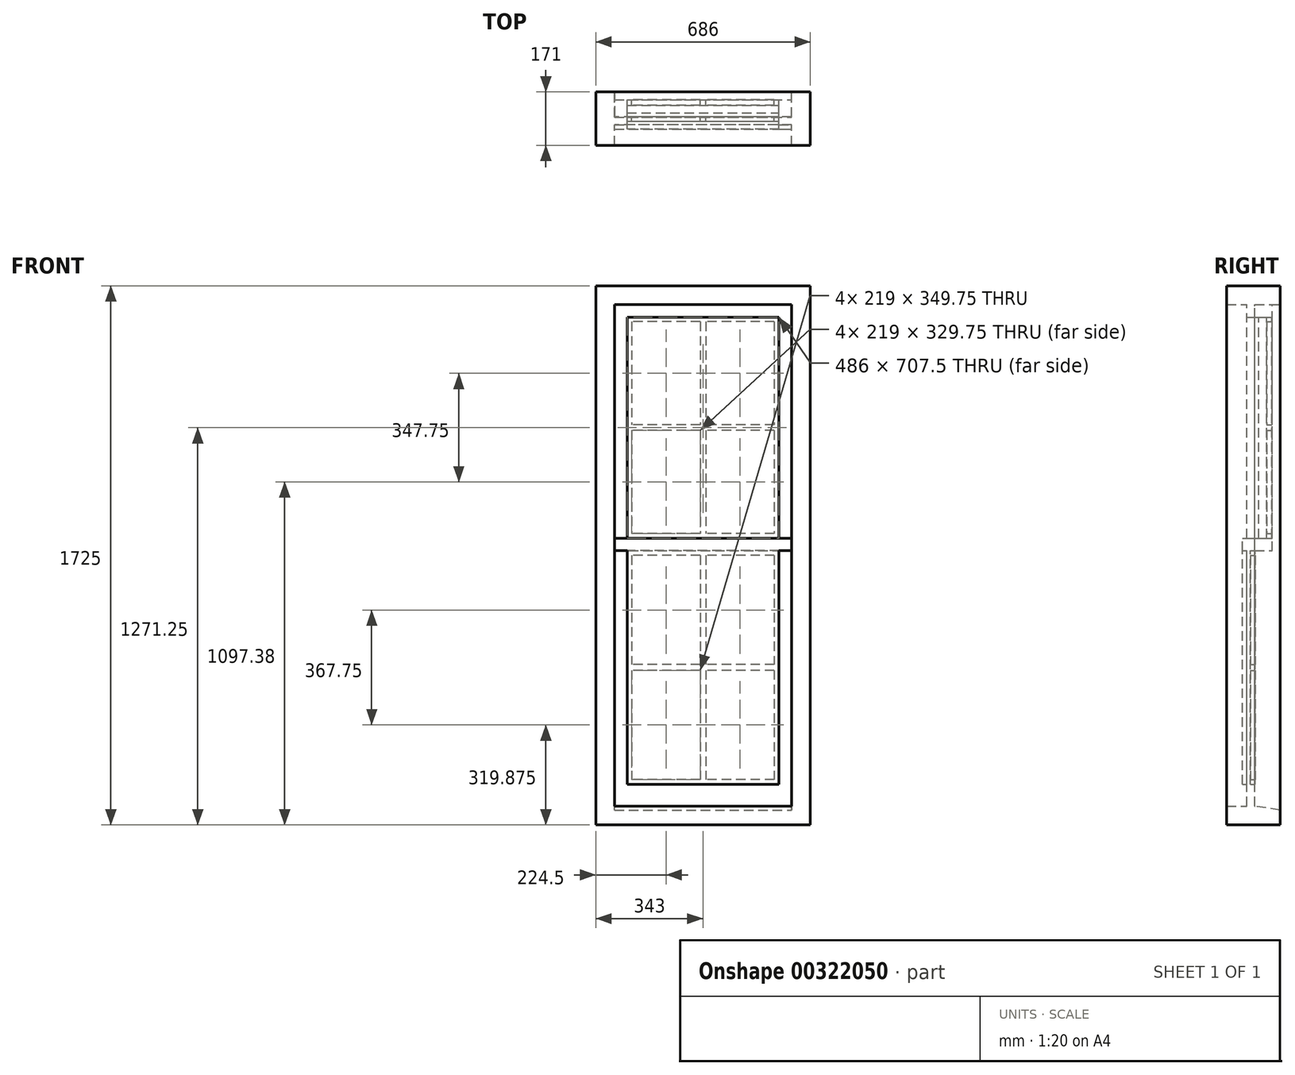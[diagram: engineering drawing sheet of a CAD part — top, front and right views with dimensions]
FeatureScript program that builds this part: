
annotation { "Feature Type Name" : "Feature", "Feature Type Description" : "" }
export const myFeature = defineFeature(function(context is Context, id is Id, definition is map)
    precondition{}
    {
        {
            var Q0;
            Q0=qCreatedBy(makeId("Front.planeOp"),FACE);
            var sketch = newSketch(context, id + "F0", { "sketchPlane" : qUnion([Q0])});
            skLineSegment(sketch, "E0.bottom", {"start": v(0, 0) * mm, "end": v(-686, 0) * mm});
            skLineSegment(sketch, "E0.top", {"start": v(0, 1725) * mm, "end": v(-686, 1725) * mm});
            skLineSegment(sketch, "E0.left", {"start": v(0, 0) * mm, "end": v(0, 1725) * mm});
            skLineSegment(sketch, "E0.right", {"start": v(-686, 0) * mm, "end": v(-686, 1725) * mm});
            skLineSegment(sketch, "E1.0", {"start": v(-60, 1665) * mm, "end": v(-626, 1665) * mm});
            skLineSegment(sketch, "E1.1", {"start": v(-60, 60) * mm, "end": v(-60, 1665) * mm});
            skLineSegment(sketch, "E1.2", {"start": v(-60, 60) * mm, "end": v(-626, 60) * mm});
            skLineSegment(sketch, "E1.3", {"start": v(-626, 60) * mm, "end": v(-626, 1665) * mm});
            skLineSegment(sketch, "E2.0", {"start": v(-586, 130) * mm, "end": v(-586, 877.5) * mm});
            skLineSegment(sketch, "E2.1", {"start": v(-100, 1625) * mm, "end": v(-586, 1625) * mm});
            skLineSegment(sketch, "E2.2", {"start": v(-100, 130) * mm, "end": v(-100, 877.5) * mm});
            skLineSegment(sketch, "E3.0", {"start": v(-100, 130) * mm, "end": v(-586, 130) * mm});
            skLineSegment(sketch, "E4", {"start": v(-626, 877.5) * mm, "end": v(-60, 877.5) * mm});
            skLineSegment(sketch, "E5.0", {"start": v(-586, 917.5) * mm, "end": v(-100, 917.5) * mm});
            skPoint(sketch, "E6.orphan", {"position": v(-100, 877.5) * mm});
            skPoint(sketch, "E7.orphan", {"position": v(-586, 877.5) * mm});
            skLineSegment(sketch, "E8.trimOffspring", {"start": v(-100, 917.5) * mm, "end": v(-100, 1625) * mm});
            skLineSegment(sketch, "E9.trimOffspring", {"start": v(-586, 917.5) * mm, "end": v(-586, 1625) * mm});
            skLineSegment(sketch, "E10.bottom", {"start": v(-115, 1610) * mm, "end": v(-334, 1610) * mm});
            skLineSegment(sketch, "E10.top", {"start": v(-115, 1280.25) * mm, "end": v(-334, 1280.25) * mm});
            skLineSegment(sketch, "E10.left", {"start": v(-115, 1610) * mm, "end": v(-115, 1280.25) * mm});
            skLineSegment(sketch, "E10.right", {"start": v(-334, 1610) * mm, "end": v(-334, 1280.25) * mm});
            skLineSegment(sketch, "E11.bottom", {"start": v(-352, 1610) * mm, "end": v(-571, 1610) * mm});
            skLineSegment(sketch, "E11.top", {"start": v(-352, 1280.25) * mm, "end": v(-571, 1280.25) * mm});
            skLineSegment(sketch, "E11.left", {"start": v(-352, 1610) * mm, "end": v(-352, 1280.25) * mm});
            skLineSegment(sketch, "E11.right", {"start": v(-571, 1610) * mm, "end": v(-571, 1280.25) * mm});
            skLineSegment(sketch, "E12.bottom", {"start": v(-115, 1262.25) * mm, "end": v(-334, 1262.25) * mm});
            skLineSegment(sketch, "E12.top", {"start": v(-115, 932.5) * mm, "end": v(-334, 932.5) * mm});
            skLineSegment(sketch, "E12.left", {"start": v(-115, 1262.25) * mm, "end": v(-115, 932.5) * mm});
            skLineSegment(sketch, "E12.right", {"start": v(-334, 1262.25) * mm, "end": v(-334, 932.5) * mm});
            skLineSegment(sketch, "E13.bottom", {"start": v(-352, 1262.25) * mm, "end": v(-571, 1262.25) * mm});
            skLineSegment(sketch, "E13.top", {"start": v(-352, 932.5) * mm, "end": v(-571, 932.5) * mm});
            skLineSegment(sketch, "E13.left", {"start": v(-352, 1262.25) * mm, "end": v(-352, 932.5) * mm});
            skLineSegment(sketch, "E13.right", {"start": v(-571, 1262.25) * mm, "end": v(-571, 932.5) * mm});
            skLineSegment(sketch, "E14.bottom", {"start": v(-115, 862.5) * mm, "end": v(-334, 862.5) * mm});
            skLineSegment(sketch, "E14.top", {"start": v(-115, 512.75) * mm, "end": v(-334, 512.75) * mm});
            skLineSegment(sketch, "E14.left", {"start": v(-115, 862.5) * mm, "end": v(-115, 512.75) * mm});
            skLineSegment(sketch, "E14.right", {"start": v(-334, 862.5) * mm, "end": v(-334, 512.75) * mm});
            skLineSegment(sketch, "E15.bottom", {"start": v(-352, 862.5) * mm, "end": v(-571, 862.5) * mm});
            skLineSegment(sketch, "E15.top", {"start": v(-352, 512.75) * mm, "end": v(-571, 512.75) * mm});
            skLineSegment(sketch, "E15.left", {"start": v(-352, 862.5) * mm, "end": v(-352, 512.75) * mm});
            skLineSegment(sketch, "E15.right", {"start": v(-571, 862.5) * mm, "end": v(-571, 512.75) * mm});
            skLineSegment(sketch, "E16.bottom", {"start": v(-115, 494.75) * mm, "end": v(-334, 494.75) * mm});
            skLineSegment(sketch, "E16.top", {"start": v(-115, 145) * mm, "end": v(-334, 145) * mm});
            skLineSegment(sketch, "E16.left", {"start": v(-115, 494.75) * mm, "end": v(-115, 145) * mm});
            skLineSegment(sketch, "E16.right", {"start": v(-334, 494.75) * mm, "end": v(-334, 145) * mm});
            skLineSegment(sketch, "E17.bottom", {"start": v(-352, 494.75) * mm, "end": v(-571, 494.75) * mm});
            skLineSegment(sketch, "E17.top", {"start": v(-352, 145) * mm, "end": v(-571, 145) * mm});
            skLineSegment(sketch, "E17.left", {"start": v(-352, 494.75) * mm, "end": v(-352, 145) * mm});
            skLineSegment(sketch, "E17.right", {"start": v(-571, 494.75) * mm, "end": v(-571, 145) * mm});
            skSolve(sketch);
        }
        {
            var Q0;
            Q0=makeQuery(id+"F0.imprint","IMPRINT",FACE,{"disambiguationData":[TD([[makeQuery(id+"F0.imprint","IMPRINT",EDGE,{"derivedFrom":sQuery(id+"F0.wireOp",EDGE,"E0.bottom")}),-1.0]])]});
            extrude(context, id + "F1", {"entities" : qUnion([Q0]), "depth" : 146 * mm, "hasSecondDirection" : true, "secondDirectionOppositeDirection" : true, "secondDirectionDepth" : 25 * mm});
        }
        {
            var Q0;
            {var subQ1=sQuery(id+"F0.wireOp",EDGE,"E1.0");Q0=makeQuery(id+"F0.imprint","IMPRINT",FACE,{"disambiguationData":[TD([[makeQuery(id+"F0.imprint","IMPRINT",EDGE,{"derivedFrom":subQ1}),1.0]])]});}
            extrude(context, id + "F2", {"entities" : qUnion([Q0]), "depth" : 56 * mm});
        }
        {
            var Q0;
            {var subQ1=sQuery(id+"F0.wireOp",EDGE,"E1.2");Q0=makeQuery(id+"F0.imprint","IMPRINT",FACE,{"disambiguationData":[TD([[makeQuery(id+"F0.imprint","IMPRINT",EDGE,{"derivedFrom":subQ1}),-1.0]])]});}
            extrude(context, id + "F3", {"entities" : qUnion([Q0]), "depth" : 81 * mm, "hasSecondDirection" : true, "secondDirectionOppositeDirection" : false, "secondDirectionDepth" : 56 * mm});
        }
        {
            var Q0;
            Q0=makeQuery(id+"F0.imprint","IMPRINT",FACE,{"disambiguationData":[TD([[makeQuery(id+"F0.imprint","IMPRINT",EDGE,{"derivedFrom":sQuery(id+"F0.wireOp",EDGE,"E2.1")}),1.0]])]});
            extrude(context, id + "F4", {"entities" : qUnion([Q0]), "depth" : 18 * mm, "hasSecondDirection" : true, "secondDirectionOppositeDirection" : false, "secondDirectionDepth" : 1 * mm});
        }
        {
            var Q0;
            {var subQ1=sQuery(id+"F0.wireOp",EDGE,"E1.2");Q0=makeQuery(id+"F0.imprint","IMPRINT",FACE,{"disambiguationData":[TD([[makeQuery(id+"F0.imprint","IMPRINT",EDGE,{"derivedFrom":subQ1}),-1.0]])]});}
            var sketch = newSketch(context, id + "F5", { "sketchPlane" : qUnion([Q0])});
            skLineSegment(sketch, "E18.bottom", {"start": v(-115, 862.5) * mm, "end": v(-334, 862.5) * mm});
            skLineSegment(sketch, "E18.top", {"start": v(-115, 512.75) * mm, "end": v(-334, 512.75) * mm});
            skLineSegment(sketch, "E18.left", {"start": v(-115, 862.5) * mm, "end": v(-115, 512.75) * mm});
            skLineSegment(sketch, "E18.right", {"start": v(-334, 862.5) * mm, "end": v(-334, 512.75) * mm});
            skLineSegment(sketch, "E19.bottom", {"start": v(-352, 862.5) * mm, "end": v(-571, 862.5) * mm});
            skLineSegment(sketch, "E19.top", {"start": v(-352, 512.75) * mm, "end": v(-571, 512.75) * mm});
            skLineSegment(sketch, "E19.left", {"start": v(-352, 862.5) * mm, "end": v(-352, 512.75) * mm});
            skLineSegment(sketch, "E19.right", {"start": v(-571, 862.5) * mm, "end": v(-571, 512.75) * mm});
            skLineSegment(sketch, "E20.bottom", {"start": v(-115, 494.75) * mm, "end": v(-334, 494.75) * mm});
            skLineSegment(sketch, "E20.top", {"start": v(-115, 145) * mm, "end": v(-334, 145) * mm});
            skLineSegment(sketch, "E20.left", {"start": v(-115, 494.75) * mm, "end": v(-115, 145) * mm});
            skLineSegment(sketch, "E20.right", {"start": v(-334, 494.75) * mm, "end": v(-334, 145) * mm});
            skLineSegment(sketch, "E21.bottom", {"start": v(-352, 494.75) * mm, "end": v(-571, 494.75) * mm});
            skLineSegment(sketch, "E21.top", {"start": v(-352, 145) * mm, "end": v(-571, 145) * mm});
            skLineSegment(sketch, "E21.left", {"start": v(-352, 494.75) * mm, "end": v(-352, 145) * mm});
            skLineSegment(sketch, "E21.right", {"start": v(-571, 494.75) * mm, "end": v(-571, 145) * mm});
            skLineSegment(sketch, "E22.bottom", {"start": v(-100, 877.5) * mm, "end": v(-586, 877.5) * mm});
            skLineSegment(sketch, "E22.top", {"start": v(-100, 130) * mm, "end": v(-586, 130) * mm});
            skLineSegment(sketch, "E22.left", {"start": v(-100, 877.5) * mm, "end": v(-100, 130) * mm});
            skLineSegment(sketch, "E22.right", {"start": v(-586, 877.5) * mm, "end": v(-586, 130) * mm});
            skSolve(sketch);
        }
        {
            var Q0;
            Q0=makeQuery(id+"F5.imprint","IMPRINT",FACE,{"disambiguationData":[TD([[makeQuery(id+"F5.imprint","IMPRINT",EDGE,{"derivedFrom":sQuery(id+"F5.wireOp",EDGE,"E18.bottom")}),-1.0]])]});
            extrude(context, id + "F6", {"entities" : qUnion([Q0]), "depth" : 70 * mm, "hasSecondDirection" : true, "secondDirectionOppositeDirection" : false, "secondDirectionDepth" : 55 * mm});
        }
        {
            var Q0;
            Q0=makeQuery(id+"F1.opExtrude","CAP_EDGE",EDGE,{"disambiguationData":[OSD([sQuery(id+"F0.wireOp",EDGE,"E1.2")])],"isStart":true});
            chamfer(context, id + "F7", {"entities" : qUnion([Q0]), "chamferType" : ChamferType.OFFSET_ANGLE, "width" : 80 * mm, "oppositeDirection" : false, "angle" : 9 * degree, "tangentPropagation" : true});
        }
        {
            var Q0;
            Q0=makeQuery(id+"F6.opExtrude","CAP_FACE",FACE,{"disambiguationData":[OSD([sQuery(id+"F5.wireOp",EDGE,"E18.bottom"),sQuery(id+"F5.wireOp",EDGE,"E18.top"),sQuery(id+"F5.wireOp",EDGE,"E18.left"),sQuery(id+"F5.wireOp",EDGE,"E18.right"),sQuery(id+"F5.wireOp",EDGE,"E19.bottom"),sQuery(id+"F5.wireOp",EDGE,"E19.top"),sQuery(id+"F5.wireOp",EDGE,"E19.left"),sQuery(id+"F5.wireOp",EDGE,"E19.right"),sQuery(id+"F5.wireOp",EDGE,"E20.bottom"),sQuery(id+"F5.wireOp",EDGE,"E20.top"),sQuery(id+"F5.wireOp",EDGE,"E20.left"),sQuery(id+"F5.wireOp",EDGE,"E20.right"),sQuery(id+"F5.wireOp",EDGE,"E21.bottom"),sQuery(id+"F5.wireOp",EDGE,"E21.top"),sQuery(id+"F5.wireOp",EDGE,"E21.left"),sQuery(id+"F5.wireOp",EDGE,"E21.right"),sQuery(id+"F5.wireOp",EDGE,"E22.bottom"),sQuery(id+"F5.wireOp",EDGE,"E22.top"),sQuery(id+"F5.wireOp",EDGE,"E22.left"),sQuery(id+"F5.wireOp",EDGE,"E22.right")])],"isStart":false});
            var sketch = newSketch(context, id + "F8", { "sketchPlane" : qUnion([Q0])});
            skLineSegment(sketch, "E23.bottom", {"start": v(-586, 877.5) * mm, "end": v(-100, 877.5) * mm});
            skLineSegment(sketch, "E23.top", {"start": v(-586, 130) * mm, "end": v(-100, 130) * mm});
            skLineSegment(sketch, "E23.left", {"start": v(-586, 877.5) * mm, "end": v(-586, 130) * mm});
            skLineSegment(sketch, "E23.right", {"start": v(-100, 877.5) * mm, "end": v(-100, 130) * mm});
            skSolve(sketch);
        }
        {
            var Q0;
            Q0=makeQuery(id+"F8.imprint","IMPRINT",FACE,{"disambiguationData":[TD([[makeQuery(id+"F8.imprint","IMPRINT",EDGE,{"derivedFrom":sQuery(id+"F8.wireOp",EDGE,"E23.bottom")}),1.0]])]});
            var Q1;
            Q1=makeQuery(id+"F8.imprint","IMPRINT",FACE,{"disambiguationData":[TD([[makeQuery(id+"F8.imprint","IMPRINT",EDGE,{"derivedFrom":makeQuery(id+"F6.opExtrude","CAP_EDGE",EDGE,{"disambiguationData":[OSD([sQuery(id+"F5.wireOp",EDGE,"E19.bottom")])],"isStart":false})}),1.0]])]});
            var Q2;
            Q2=makeQuery(id+"F8.imprint","IMPRINT",FACE,{"disambiguationData":[TD([[makeQuery(id+"F8.imprint","IMPRINT",EDGE,{"derivedFrom":makeQuery(id+"F6.opExtrude","CAP_EDGE",EDGE,{"disambiguationData":[OSD([sQuery(id+"F5.wireOp",EDGE,"E18.bottom")])],"isStart":false})}),1.0]])]});
            var Q3;
            Q3=makeQuery(id+"F8.imprint","IMPRINT",FACE,{"disambiguationData":[TD([[makeQuery(id+"F8.imprint","IMPRINT",EDGE,{"derivedFrom":makeQuery(id+"F6.opExtrude","CAP_EDGE",EDGE,{"disambiguationData":[OSD([sQuery(id+"F5.wireOp",EDGE,"E21.bottom")])],"isStart":false})}),1.0]])]});
            var Q4;
            Q4=makeQuery(id+"F8.imprint","IMPRINT",FACE,{"disambiguationData":[TD([[makeQuery(id+"F8.imprint","IMPRINT",EDGE,{"derivedFrom":makeQuery(id+"F6.opExtrude","CAP_EDGE",EDGE,{"disambiguationData":[OSD([sQuery(id+"F5.wireOp",EDGE,"E20.bottom")])],"isStart":false})}),1.0]])]});
            extrude(context, id + "F9", {"entities" : qUnion([Q0, Q1, Q2, Q3, Q4]), "depth" : 25 * mm});
        }
        {
            var Q0;
            Q0=makeQuery(id+"F2.opExtrude","CAP_FACE",FACE,{"disambiguationData":[OSD([sQuery(id+"F0.wireOp",EDGE,"E1.0"),sQuery(id+"F0.wireOp",EDGE,"E1.1"),sQuery(id+"F0.wireOp",EDGE,"E1.3"),sQuery(id+"F0.wireOp",EDGE,"E2.1"),sQuery(id+"F0.wireOp",EDGE,"E4"),sQuery(id+"F0.wireOp",EDGE,"E5.0"),sQuery(id+"F0.wireOp",EDGE,"E8.trimOffspring"),sQuery(id+"F0.wireOp",EDGE,"E9.trimOffspring")])],"isStart":false});
            extrude(context, id + "F10", {"entities" : qUnion([Q0]), "depth" : 25 * mm});
        }
        {
            var Q0;
            Q0=makeQuery(id+"F10.opExtrude","CAP_FACE",FACE,{"disambiguationData":[OSD([sQuery(id+"F0.wireOp",EDGE,"E1.0"),sQuery(id+"F0.wireOp",EDGE,"E1.1"),sQuery(id+"F0.wireOp",EDGE,"E1.3"),sQuery(id+"F0.wireOp",EDGE,"E2.1"),sQuery(id+"F0.wireOp",EDGE,"E4"),sQuery(id+"F0.wireOp",EDGE,"E5.0"),sQuery(id+"F0.wireOp",EDGE,"E8.trimOffspring"),sQuery(id+"F0.wireOp",EDGE,"E9.trimOffspring")])],"isStart":false});
            var sketch = newSketch(context, id + "F11", { "sketchPlane" : qUnion([Q0])});
            skLineSegment(sketch, "E24", {"start": v(-586, 917.5) * mm, "end": v(-626, 917.5) * mm});
            skLineSegment(sketch, "E25", {"start": v(-100, 917.5) * mm, "end": v(-60, 917.5) * mm});
            skSolve(sketch);
        }
        {
            var Q0;
            {var subQ2=sQuery(id+"F11.wireOp",EDGE,"E24");Q0=makeQuery(id+"F11.imprint","IMPRINT",FACE,{"disambiguationData":[TD([[makeQuery(id+"F11.imprint","IMPRINT",EDGE,{"derivedFrom":subQ2}),1.0]])]});}
            var Q1;
            Q1=makeQuery(id+"F9.opExtrude","CAP_FACE",FACE,{"disambiguationData":[OSD([sQuery(id+"F8.wireOp",EDGE,"E23.bottom"),sQuery(id+"F8.wireOp",EDGE,"E23.top"),sQuery(id+"F8.wireOp",EDGE,"E23.left"),sQuery(id+"F8.wireOp",EDGE,"E23.right")])],"isStart":false});
            extrude(context, id + "F12", {"entities" : qUnion([Q0]), "operationType" : NewBodyOperationType.ADD, "endBound" : BoundingType.UP_TO_SURFACE, "endBoundEntityFace" : qUnion([Q1]), "depth" : 25 * mm});
        }
        {
            var Q0;
            Q0=makeQuery(id+"F4.opExtrude","CAP_FACE",FACE,{"disambiguationData":[OSD([sQuery(id+"F0.wireOp",EDGE,"E2.1"),sQuery(id+"F0.wireOp",EDGE,"E5.0"),sQuery(id+"F0.wireOp",EDGE,"E8.trimOffspring"),sQuery(id+"F0.wireOp",EDGE,"E9.trimOffspring"),sQuery(id+"F0.wireOp",EDGE,"E10.bottom"),sQuery(id+"F0.wireOp",EDGE,"E10.top"),sQuery(id+"F0.wireOp",EDGE,"E10.left"),sQuery(id+"F0.wireOp",EDGE,"E10.right"),sQuery(id+"F0.wireOp",EDGE,"E11.bottom"),sQuery(id+"F0.wireOp",EDGE,"E11.top"),sQuery(id+"F0.wireOp",EDGE,"E11.left"),sQuery(id+"F0.wireOp",EDGE,"E11.right"),sQuery(id+"F0.wireOp",EDGE,"E12.bottom"),sQuery(id+"F0.wireOp",EDGE,"E12.top"),sQuery(id+"F0.wireOp",EDGE,"E12.left"),sQuery(id+"F0.wireOp",EDGE,"E12.right"),sQuery(id+"F0.wireOp",EDGE,"E13.bottom"),sQuery(id+"F0.wireOp",EDGE,"E13.top"),sQuery(id+"F0.wireOp",EDGE,"E13.left"),sQuery(id+"F0.wireOp",EDGE,"E13.right")])],"isStart":false});
            var sketch = newSketch(context, id + "F13", { "sketchPlane" : qUnion([Q0])});
            skLineSegment(sketch, "E26.bottom", {"start": v(-586, 1625) * mm, "end": v(-100, 1625) * mm});
            skLineSegment(sketch, "E26.top", {"start": v(-586, 917.5) * mm, "end": v(-100, 917.5) * mm});
            skLineSegment(sketch, "E26.left", {"start": v(-586, 1625) * mm, "end": v(-586, 917.5) * mm});
            skLineSegment(sketch, "E26.right", {"start": v(-100, 1625) * mm, "end": v(-100, 917.5) * mm});
            skSolve(sketch);
        }
        {
            var Q0;
            Q0=makeQuery(id+"F13.imprint","IMPRINT",FACE,{"disambiguationData":[TD([[makeQuery(id+"F13.imprint","IMPRINT",EDGE,{"derivedFrom":sQuery(id+"F13.wireOp",EDGE,"E26.bottom")}),1.0]])]});
            var Q1;
            Q1=makeQuery(id+"F13.imprint","IMPRINT",FACE,{"disambiguationData":[TD([[makeQuery(id+"F13.imprint","IMPRINT",EDGE,{"derivedFrom":makeQuery(id+"F4.opExtrude","CAP_EDGE",EDGE,{"disambiguationData":[OSD([sQuery(id+"F0.wireOp",EDGE,"E12.bottom")])],"isStart":false})}),1.0]])]});
            var Q2;
            Q2=makeQuery(id+"F13.imprint","IMPRINT",FACE,{"disambiguationData":[TD([[makeQuery(id+"F13.imprint","IMPRINT",EDGE,{"derivedFrom":makeQuery(id+"F4.opExtrude","CAP_EDGE",EDGE,{"disambiguationData":[OSD([sQuery(id+"F0.wireOp",EDGE,"E13.bottom")])],"isStart":false})}),1.0]])]});
            var Q3;
            Q3=makeQuery(id+"F13.imprint","IMPRINT",FACE,{"disambiguationData":[TD([[makeQuery(id+"F13.imprint","IMPRINT",EDGE,{"derivedFrom":makeQuery(id+"F4.opExtrude","CAP_EDGE",EDGE,{"disambiguationData":[OSD([sQuery(id+"F0.wireOp",EDGE,"E11.bottom")])],"isStart":false})}),1.0]])]});
            var Q4;
            Q4=makeQuery(id+"F13.imprint","IMPRINT",FACE,{"disambiguationData":[TD([[makeQuery(id+"F13.imprint","IMPRINT",EDGE,{"derivedFrom":makeQuery(id+"F4.opExtrude","CAP_EDGE",EDGE,{"disambiguationData":[OSD([sQuery(id+"F0.wireOp",EDGE,"E10.bottom")])],"isStart":false})}),1.0]])]});
            extrude(context, id + "F14", {"entities" : qUnion([Q0, Q1, Q2, Q3, Q4]), "depth" : 25 * mm});
        }
    });
